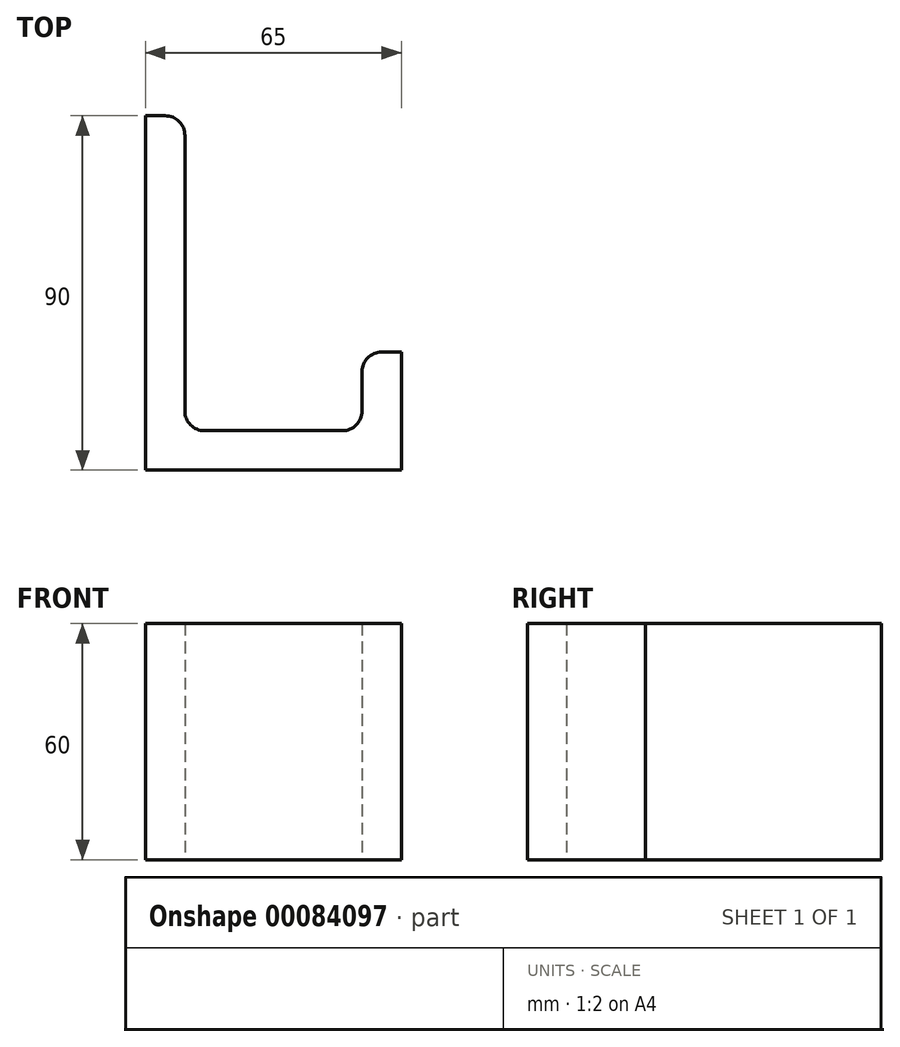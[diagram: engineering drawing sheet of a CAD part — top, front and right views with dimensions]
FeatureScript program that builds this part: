
annotation { "Feature Type Name" : "Feature", "Feature Type Description" : "" }
export const myFeature = defineFeature(function(context is Context, id is Id, definition is map)
    precondition{}
    {
        {
            var Q0;
            Q0=qCreatedBy(makeId("Top.planeOp"),FACE);
            var sketch = newSketch(context, id + "F0", { "sketchPlane" : qUnion([Q0])});
            skLineSegment(sketch, "E0.bottom", {"start": v(0, 0) * mm, "end": v(-65, 0) * mm});
            skLineSegment(sketch, "E0.top", {"start": v(0, 10) * mm, "end": v(-65, 10) * mm});
            skLineSegment(sketch, "E0.left", {"start": v(0, 0) * mm, "end": v(0, 10) * mm});
            skLineSegment(sketch, "E0.right", {"start": v(-65, 0) * mm, "end": v(-65, 10) * mm});
            skLineSegment(sketch, "E1.bottom", {"start": v(-65, 10) * mm, "end": v(-55, 10) * mm});
            skLineSegment(sketch, "E1.top", {"start": v(-65, 90) * mm, "end": v(-55, 90) * mm});
            skLineSegment(sketch, "E1.left", {"start": v(-65, 10) * mm, "end": v(-65, 90) * mm});
            skLineSegment(sketch, "E1.right", {"start": v(-55, 10) * mm, "end": v(-55, 90) * mm});
            skLineSegment(sketch, "E2.bottom", {"start": v(0, 10) * mm, "end": v(-10, 10) * mm});
            skLineSegment(sketch, "E2.top", {"start": v(0, 30) * mm, "end": v(-10, 30) * mm});
            skLineSegment(sketch, "E2.left", {"start": v(0, 10) * mm, "end": v(0, 30) * mm});
            skLineSegment(sketch, "E2.right", {"start": v(-10, 10) * mm, "end": v(-10, 30) * mm});
            skSolve(sketch);
        }
        {
            var Q0;
            Q0 = qSketchRegion(id + "F0", true);
            extrude(context, id + "F1", {"entities" : qUnion([Q0]), "depth" : 60 * mm, "offsetDistance" : 25 * mm});
        }
        {
            var Q0;
            Q0=makeQuery(id+"F1.opExtrude","SWEPT_EDGE",EDGE,{"disambiguationData":[OSD([sQuery(id+"F0.wireOp",EDGE,"E0.top"),sQuery(id+"F0.wireOp",EDGE,"E1.right")])]});
            var Q1;
            Q1=makeQuery(id+"F1.opExtrude","SWEPT_EDGE",EDGE,{"disambiguationData":[OSD([sQuery(id+"F0.wireOp",EDGE,"E0.top"),sQuery(id+"F0.wireOp",EDGE,"E2.right")])]});
            var Q2;
            Q2=makeQuery(id+"F1.opExtrude","SWEPT_EDGE",EDGE,{"disambiguationData":[OSD([sQuery(id+"F0.wireOp",EDGE,"E1.top"),sQuery(id+"F0.wireOp",EDGE,"E1.right")])]});
            var Q3;
            Q3=makeQuery(id+"F1.opExtrude","SWEPT_EDGE",EDGE,{"disambiguationData":[OSD([sQuery(id+"F0.wireOp",EDGE,"E2.top"),sQuery(id+"F0.wireOp",EDGE,"E2.right")])]});
            fillet(context, id + "F2", {"entities" : qUnion([Q0, Q1, Q2, Q3]), "tangentPropagation" : true, "radius" : 5 * mm, "defaultsChanged" : false, "vertexSettings" : [], "allowEdgeOverflow" : false});
        }
    });
